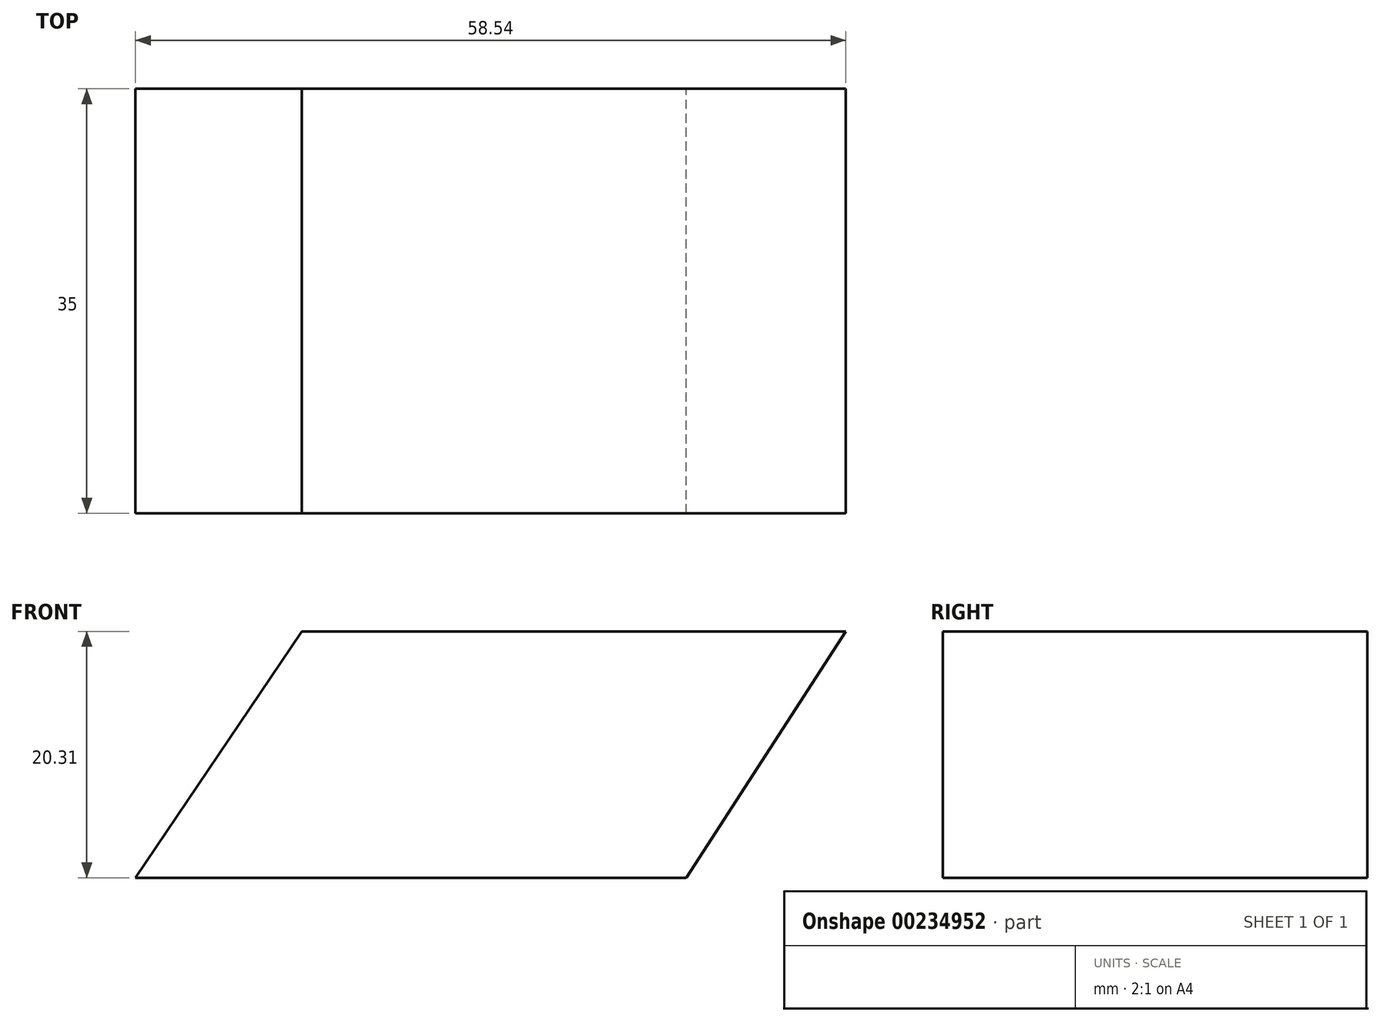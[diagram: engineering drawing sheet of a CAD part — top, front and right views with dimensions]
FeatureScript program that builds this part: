
annotation { "Feature Type Name" : "Feature", "Feature Type Description" : "" }
export const myFeature = defineFeature(function(context is Context, id is Id, definition is map)
    precondition{}
    {
        {
            var Q0;
            Q0=qCreatedBy(makeId("Front.planeOp"),FACE);
            var sketch = newSketch(context, id + "F0", { "sketchPlane" : qUnion([Q0])});
            skLineSegment(sketch, "E0", {"start": v(0, 0) * mm, "end": v(0, 39.26) * mm});
            skLineSegment(sketch, "E1", {"start": v(0, 39.26) * mm, "end": v(13.32, 56.94) * mm});
            skLineSegment(sketch, "E2", {"start": v(13.32, 56.94) * mm, "end": v(67.73, 53.5) * mm});
            skLineSegment(sketch, "E3", {"start": v(67.73, 53.5) * mm, "end": v(77.6, 39.26) * mm});
            skLineSegment(sketch, "E4", {"start": v(-74.85, 0) * mm, "end": v(-74.85, 42.34) * mm});
            skLineSegment(sketch, "E5", {"start": v(-74.85, 42.34) * mm, "end": v(-61.13, 62.65) * mm});
            skLineSegment(sketch, "E6", {"start": v(-61.13, 62.65) * mm, "end": v(-16.31, 62.65) * mm});
            skLineSegment(sketch, "E7", {"start": v(-16.31, 62.65) * mm, "end": v(-29.46, 42.34) * mm});
            skLineSegment(sketch, "E8", {"start": v(-29.46, 42.34) * mm, "end": v(-74.85, 42.34) * mm});
            skSolve(sketch);
        }
        {
            var Q0;
            Q0=makeQuery(id+"F0.imprint","IMPRINT",FACE,{"disambiguationData":[TD([[makeQuery(id+"F0.imprint","IMPRINT",EDGE,{"derivedFrom":sQuery(id+"F0.wireOp",EDGE,"E5")}),-1.0]])]});
            extrude(context, id + "F1", {"entities" : qUnion([Q0]), "depth" : 25 * mm});
        }
        {
            var Q0;
            Q0=makeQuery(id+"F1.opExtrude","CAP_FACE",FACE,{"disambiguationData":[OSD([sQuery(id+"F0.wireOp",EDGE,"E5"),sQuery(id+"F0.wireOp",EDGE,"E6"),sQuery(id+"F0.wireOp",EDGE,"E7"),sQuery(id+"F0.wireOp",EDGE,"E8")])],"isStart":false});
            extrude(context, id + "F2", {"entities" : qUnion([Q0]), "operationType" : NewBodyOperationType.ADD, "depth" : 10 * mm, "hasSecondDirection" : true, "secondDirectionOppositeDirection" : true, "secondDirectionDepth" : 10 * mm});
        }
    });
